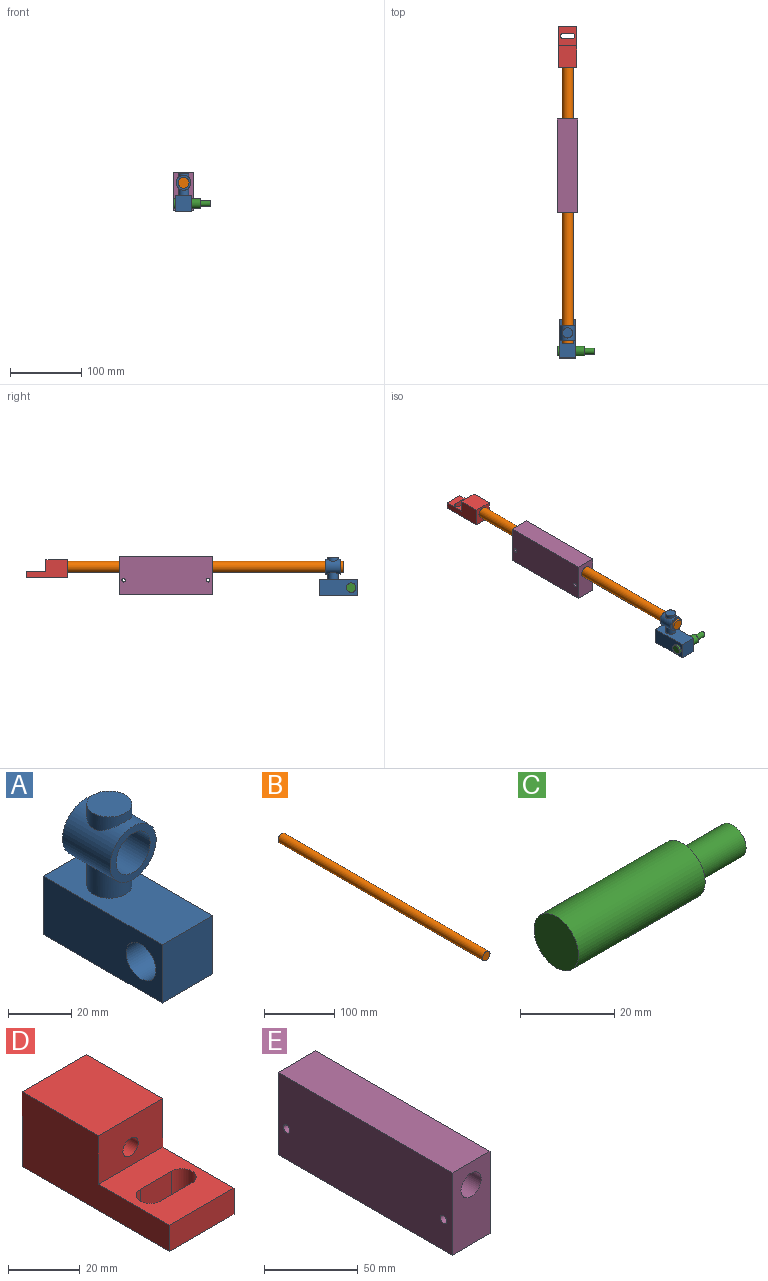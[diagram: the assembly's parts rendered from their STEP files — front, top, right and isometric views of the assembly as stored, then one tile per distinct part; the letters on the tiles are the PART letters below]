
ASSEMBLY  parts=5 mates=4
PART A: 18 faces, bbox 22.6x53.3x54.1 mm
  f0: plane 53.34x22.61mm, normal (0,0,1), area 1045.3mm2, adj f1,f4,f5,f6,f12
  f1: plane 22.61x22.61mm, normal (0,-1,0), area 511mm2, adj f0,f2,f5,f6
  f2: plane 53.34x22.61mm, normal (0,0,-1), area 1205.8mm2, adj f1,f4,f5,f6
  f3: cylinder r=6.69mm len=22.61mm, axis (-1,0,0), area 950.7mm2, adj f5,f6
  f4: plane 22.61x22.61mm, normal (0,1,0), area 511mm2, adj f0,f2,f5,f6
  f5: plane 53.34x22.61mm, normal (1,0,0), area 1065.1mm2, adj f0,f1,f2,f3,f4
  f6: plane 53.34x22.61mm, normal (-1,0,0), area 1065.1mm2, adj f0,f1,f2,f3,f4
  f7: cylinder r=10.34mm len=21.33mm, axis (0,1,0), area 1042.3mm2, adj f8,f10,f11,f12,f13,f14,f15,f16
  f8: plane 20.68x20.68mm, normal (0,-1,0), area 153.4mm2, adj f7,f9
  f9: cylinder r=7.62mm len=21.33mm, axis (0,1,0), area 1021.1mm2, adj f8,f10
  f10: plane 20.68x20.68mm, normal (0,1,0), area 153.4mm2, adj f7,f9
  f11: plane 3.01x0.16mm, normal (0,0,1), area 0.3mm2, adj f7,f12
  f12: cylinder r=7.15mm len=14.3mm, axis (0,0,-1), area 401.1mm2, adj f0,f7,f11,f13
  f13: plane 3.01x0.16mm, normal (0,0,1), area 0.3mm2, adj f7,f12
  f14: plane 3.01x0.16mm, normal (0,0,-1), area 0.3mm2, adj f7,f15
  f15: cylinder r=7.15mm len=14.3mm, axis (0,0,-1), area 208.3mm2, adj f7,f14,f16,f17
  f16: plane 3.01x0.16mm, normal (0,0,-1), area 0.3mm2, adj f7,f15
  f17: plane 14.3x14.3mm, normal (0,0,1), area 160.5mm2, adj f15
PART B: 3 faces, bbox 15.2x411.5x15.2 mm
  f0: cylinder r=7.62mm len=411.48mm, axis (0,1,0), area 19700.8mm2, adj f1,f2
  f1: plane 15.24x15.24mm, normal (0,-1,0), area 182.4mm2, adj f0
  f2: plane 15.24x15.24mm, normal (0,1,0), area 182.4mm2, adj f0
PART C: 5 faces, bbox 53.1x13.4x13.4 mm
  f0: cylinder r=6.69mm len=38.1mm, axis (-1,0,0), area 1602.3mm2, adj f1,f2
  f1: plane 13.39x13.39mm, normal (1,0,0), area 90.5mm2, adj f0,f3
  f2: plane 13.39x13.39mm, normal (-1,0,0), area 140.7mm2, adj f0
  f3: cylinder r=4mm len=15mm, axis (-1,0,0), area 377mm2, adj f1,f4
  f4: plane 8x8mm, normal (1,0,0), area 50.3mm2, adj f3
PART D: 15 faces, bbox 25.4x57.9x25.4 mm
  f0: plane 25.4x25.4mm, normal (0,1,0), area 462.7mm2, adj f1,f5,f6,f7,f8
  f1: plane 29.97x25.4mm, normal (0,0,1), area 761.3mm2, adj f0,f2,f6,f7
  f2: plane 25.4x16.49mm, normal (0,-1,0), area 390.5mm2, adj f1,f3,f6,f7,f10
  f3: plane 27.94x25.4mm, normal (0,0,1), area 560.9mm2, adj f2,f4,f6,f7,f11,f12,f13,f14
  f4: plane 25.4x8.91mm, normal (0,-1,0), area 226.4mm2, adj f3,f5,f6,f7
  f5: plane 57.91x25.4mm, normal (0,0,-1), area 1322.1mm2, adj f0,f4,f6,f7,f11,f12,f13,f14
  f6: plane 57.91x25.4mm, normal (1,0,0), area 1010.3mm2, adj f0,f1,f2,f3,f4,f5
  f7: plane 57.91x25.4mm, normal (-1,0,0), area 1010.3mm2, adj f0,f1,f2,f3,f4,f5
  f8: cylinder r=7.62mm len=25.4mm, axis (0,1,0), area 1216.1mm2, adj f0,f9
  f9: plane 15.24x15.24mm, normal (0,1,0), area 154.1mm2, adj f8,f10
  f10: cylinder r=3mm len=6mm, axis (0,-1,0), area 86.2mm2, adj f2,f9
  f11: plane 12.32x8.91mm, normal (0,-1,0), area 109.8mm2, adj f3,f5,f12,f14
  f12: cylinder r=4mm len=8.91mm, axis (0,0,1), area 112mm2, adj f3,f5,f11,f13
  f13: plane 12.32x8.91mm, normal (0,1,0), area 109.8mm2, adj f3,f5,f12,f14
  f14: cylinder r=4mm len=8.91mm, axis (0,0,1), area 112mm2, adj f3,f5,f11,f13
PART E: 9 faces, bbox 28.4x131.1x53.6 mm
  f0: plane 53.59x28.45mm, normal (0,1,0), area 1342.2mm2, adj f1,f4,f6,f7,f8
  f1: plane 131.06x28.45mm, normal (0,0,1), area 3728.5mm2, adj f0,f2,f6,f7
  f2: plane 53.59x28.45mm, normal (0,-1,0), area 1342.2mm2, adj f1,f4,f6,f7,f8
  f3: cylinder r=2.5mm len=28.45mm, axis (-1,0,0), area 447mm2, adj f6,f7
  f4: plane 131.06x28.45mm, normal (0,0,-1), area 3728.5mm2, adj f0,f2,f6,f7
  f5: cylinder r=2.5mm len=28.45mm, axis (-1,0,0), area 447mm2, adj f6,f7
  f6: plane 131.06x53.59mm, normal (1,0,0), area 6985mm2, adj f0,f1,f2,f3,f4,f5
  f7: plane 131.06x53.59mm, normal (-1,0,0), area 6985mm2, adj f0,f1,f2,f3,f4,f5
  f8: cylinder r=7.62mm len=131.06mm, axis (0,1,0), area 6275.1mm2, adj f0,f2
PLACE A t=(-33.58,-35.23,-7.77)mm
PLACE B rot(axis=(1,0,0),180deg) t=(-33.58,-16.35,-7.77)mm fixed
PLACE C t=(-35.64,-35.23,-7.77)mm
PLACE D rot(axis=(0,0,1),180deg) t=(-33.58,190.53,-16.38)mm
PLACE E t=(-33.58,26.09,-7.77)mm
MATE slider B.f0 <-> E.f8  axis (0,-1,0) through (-33.58,-16.35,-7.77)mm
MATE slider C.f0 <-> A.f3  axis (-1,0,0) through (-48.34,-233.48,-36.98)mm
MATE slider A.f7 <-> B.f0  axis (0,-1,0) through (-33.58,-218.61,-7.77)mm
MATE fastened D.f8 <-> B.f0  axis (0,-1,0) through (-33.58,189.39,-7.77)mm
